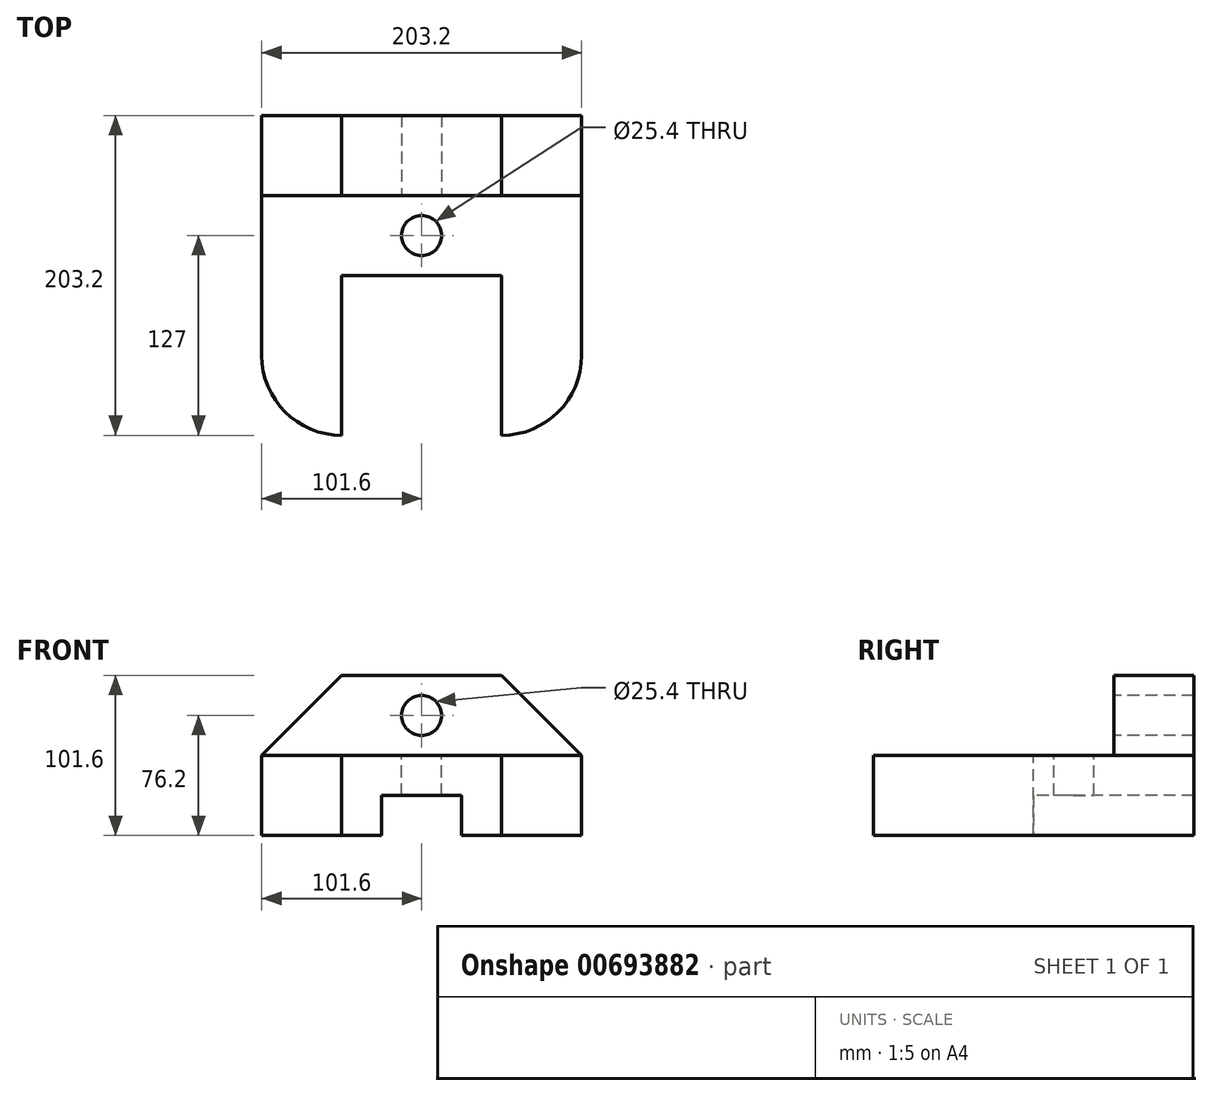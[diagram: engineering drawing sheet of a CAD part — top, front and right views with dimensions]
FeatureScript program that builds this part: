
annotation { "Feature Type Name" : "Feature", "Feature Type Description" : "" }
export const myFeature = defineFeature(function(context is Context, id is Id, definition is map)
    precondition{}
    {
        {
            var Q0;
            Q0=qCreatedBy(makeId("Front.planeOp"),FACE);
            var sketch = newSketch(context, id + "F0", { "sketchPlane" : qUnion([Q0])});
            skLineSegment(sketch, "E0.bottom", {"start": v(-101.6, -50.8) * mm, "end": v(101.6, -50.8) * mm});
            skLineSegment(sketch, "E0.top", {"start": v(-50.8, 50.8) * mm, "end": v(50.8, 50.8) * mm});
            skLineSegment(sketch, "E0.left", {"start": v(-101.6, -50.8) * mm, "end": v(-101.6, 0) * mm});
            skLineSegment(sketch, "E0.right", {"start": v(101.6, -50.8) * mm, "end": v(101.6, 0) * mm});
            skPoint(sketch, "E0.middle", {"position": v(0, 0) * mm});
            skLineSegment(sketch, "E1.0", {"start": v(-101.6, 0) * mm, "end": v(101.6, 0) * mm});
            skCircle(sketch, "E2", {"center": v(0, 25.4) * mm, "radius": 12.7 * mm});
            skLineSegment(sketch, "E3.0", {"start": v(-50.8, -50.8) * mm, "end": v(-50.8, 0) * mm});
            skLineSegment(sketch, "E4.0", {"start": v(50.8, -50.8) * mm, "end": v(50.8, 0) * mm});
            skLineSegment(sketch, "E5.0", {"start": v(25.4, -25.4) * mm, "end": v(25.4, -25.4) * mm});
            skLineSegment(sketch, "E6.0", {"start": v(-25.4, -25.4) * mm, "end": v(25.4, -25.4) * mm});
            skLineSegment(sketch, "E7", {"start": v(-25.4, -25.4) * mm, "end": v(-25.4, -50.8) * mm});
            skLineSegment(sketch, "E8", {"start": v(25.4, -25.4) * mm, "end": v(25.4, -50.8) * mm});
            skLineSegment(sketch, "E9", {"start": v(-101.6, 0) * mm, "end": v(-50.8, 50.8) * mm});
            skLineSegment(sketch, "E10", {"start": v(-50.8, 50.8) * mm, "end": v(-50.8, 0) * mm});
            skLineSegment(sketch, "E11", {"start": v(-50.8, 0) * mm, "end": v(-101.6, 0) * mm});
            skLineSegment(sketch, "E12.MirrorCS", {"start": v(50.8, 50.8) * mm, "end": v(50.8, 0) * mm});
            skLineSegment(sketch, "E13.MirrorCS", {"start": v(101.6, 0) * mm, "end": v(50.8, 50.8) * mm});
            skPoint(sketch, "E14.orphan", {"position": v(-101.6, 50.8) * mm});
            skPoint(sketch, "E15.orphan", {"position": v(101.6, 50.8) * mm});
            skSolve(sketch);
        }
        {
            var Q0;
            Q0=qCreatedBy(makeId("Top.planeOp"),FACE);
            var sketch = newSketch(context, id + "F1", { "sketchPlane" : qUnion([Q0])});
            skLineSegment(sketch, "E16.bottom", {"start": v(-50.8, -101.6) * mm, "end": v(-50.8, -101.6) * mm});
            skLineSegment(sketch, "E16.top", {"start": v(-101.6, 101.6) * mm, "end": v(101.6, 101.6) * mm});
            skLineSegment(sketch, "E16.left", {"start": v(-101.6, -50.8) * mm, "end": v(-101.6, 101.6) * mm});
            skLineSegment(sketch, "E16.right", {"start": v(101.6, -50.8) * mm, "end": v(101.6, 101.6) * mm});
            skPoint(sketch, "E16.middle", {"position": v(0, 0) * mm});
            skLineSegment(sketch, "E17.0", {"start": v(-101.6, 50.8) * mm, "end": v(101.6, 50.8) * mm});
            skLineSegment(sketch, "E18.0", {"start": v(-50.8, 0) * mm, "end": v(50.8, 0) * mm});
            skLineSegment(sketch, "E19.0", {"start": v(-50.8, -101.6) * mm, "end": v(-50.8, 0) * mm});
            skArc(sketch, "E20", {"start": v(-101.6, -50.28) * mm, "mid": v(-86.9, -86.54) * mm, "end": v(-50.8, -101.6) * mm});
            skArc(sketch, "E21.MirrorCS", {"start": v(101.6, -50.28) * mm, "mid": v(86.9, -86.54) * mm, "end": v(50.8, -101.6) * mm});
            skLineSegment(sketch, "E22.trimOffspring", {"start": v(-50.8, 50.8) * mm, "end": v(-50.8, 101.6) * mm});
            skPoint(sketch, "E23.orphan", {"position": v(-101.6, -101.6) * mm});
            skLineSegment(sketch, "E24", {"start": v(50.8, -101.6) * mm, "end": v(50.8, -50.8) * mm});
            skLineSegment(sketch, "E25", {"start": v(50.8, 0) * mm, "end": v(-50.8, 0) * mm});
            skLineSegment(sketch, "E26", {"start": v(50.8, 0) * mm, "end": v(50.8, -50.8) * mm});
            skPoint(sketch, "E27.orphan", {"position": v(101.6, -101.6) * mm});
            skLineSegment(sketch, "E28.trimOffspring", {"start": v(50.8, -101.6) * mm, "end": v(50.8, -101.6) * mm});
            skLineSegment(sketch, "E29.MirrorCS", {"start": v(50.8, 50.8) * mm, "end": v(50.8, 101.6) * mm});
            skCircle(sketch, "E30", {"center": v(0, 25.4) * mm, "radius": 12.7 * mm});
            skSolve(sketch);
        }
        {
            var Q0;
            {var subQ7=sQuery(id+"F1.wireOp",EDGE,"E19.0");Q0=makeQuery(id+"F1.imprint","IMPRINT",FACE,{"disambiguationData":[TD([[makeQuery(id+"F1.imprint","IMPRINT",EDGE,{"derivedFrom":subQ7}),1.0]])]});}
            var Q1;
            {var subQ3=sQuery(id+"F1.wireOp",EDGE,"E22.trimOffspring");Q1=makeQuery(id+"F1.imprint","IMPRINT",FACE,{"disambiguationData":[TD([[makeQuery(id+"F1.imprint","IMPRINT",EDGE,{"derivedFrom":subQ3}),1.0]])]});}
            var Q2;
            {var subQ0=sQuery(id+"F1.wireOp",EDGE,"E22.trimOffspring");Q2=makeQuery(id+"F1.imprint","IMPRINT",FACE,{"disambiguationData":[TD([[makeQuery(id+"F1.imprint","IMPRINT",EDGE,{"derivedFrom":subQ0}),-1.0]])]});}
            var Q3;
            {var subQ3=sQuery(id+"F1.wireOp",EDGE,"E29.MirrorCS");Q3=makeQuery(id+"F1.imprint","IMPRINT",FACE,{"disambiguationData":[TD([[makeQuery(id+"F1.imprint","IMPRINT",EDGE,{"derivedFrom":subQ3}),-1.0]])]});}
            extrude(context, id + "F2", {"entities" : qUnion([Q0, Q1, Q2, Q3]), "oppositeDirection" : true, "depth" : 50.8 * mm, "offsetDistance" : 25.4 * mm});
        }
        {
            var Q0;
            Q0=makeQuery(id+"F0.imprint","IMPRINT",FACE,{"disambiguationData":[TD([[makeQuery(id+"F0.imprint","IMPRINT",EDGE,{"derivedFrom":sQuery(id+"F0.wireOp",EDGE,"E9")}),-1.0]])]});
            var Q1;
            Q1=makeQuery(id+"F0.imprint","IMPRINT",FACE,{"disambiguationData":[TD([[makeQuery(id+"F0.imprint","IMPRINT",EDGE,{"derivedFrom":sQuery(id+"F0.wireOp",EDGE,"E0.top")}),-1.0]])]});
            var Q2;
            {var subQ2=sQuery(id+"F0.wireOp",EDGE,"E12.MirrorCS");Q2=makeQuery(id+"F0.imprint","IMPRINT",FACE,{"disambiguationData":[TD([[makeQuery(id+"F0.imprint","IMPRINT",EDGE,{"derivedFrom":subQ2}),1.0]])]});}
            extrude(context, id + "F3", {"entities" : qUnion([Q0, Q1, Q2]), "operationType" : NewBodyOperationType.ADD, "oppositeDirection" : true, "depth" : 101.6 * mm, "offsetDistance" : 25.4 * mm});
        }
        {
            var Q0;
            Q0=makeQuery(id+"F0.imprint","IMPRINT",FACE,{"disambiguationData":[TD([[makeQuery(id+"F0.imprint","IMPRINT",EDGE,{"derivedFrom":sQuery(id+"F0.wireOp",EDGE,"E0.top")}),-1.0]])]});
            var Q1;
            Q1=makeQuery(id+"F0.imprint","IMPRINT",FACE,{"disambiguationData":[TD([[makeQuery(id+"F0.imprint","IMPRINT",EDGE,{"derivedFrom":sQuery(id+"F0.wireOp",EDGE,"E9")}),-1.0]])]});
            var Q2;
            {var subQ2=sQuery(id+"F0.wireOp",EDGE,"E12.MirrorCS");Q2=makeQuery(id+"F0.imprint","IMPRINT",FACE,{"disambiguationData":[TD([[makeQuery(id+"F0.imprint","IMPRINT",EDGE,{"derivedFrom":subQ2}),1.0]])]});}
            extrude(context, id + "F4", {"entities" : qUnion([Q0, Q1, Q2]), "operationType" : NewBodyOperationType.REMOVE, "oppositeDirection" : true, "depth" : 50.8 * mm, "offsetDistance" : 25.4 * mm});
        }
        {
            var Q0;
            Q0=makeQuery(id+"F0.imprint","IMPRINT",FACE,{"disambiguationData":[TD([[makeQuery(id+"F0.imprint","IMPRINT",EDGE,{"derivedFrom":sQuery(id+"F0.wireOp",EDGE,"E6.0")}),-1.0]])]});
            extrude(context, id + "F5", {"entities" : qUnion([Q0]), "operationType" : NewBodyOperationType.REMOVE, "oppositeDirection" : true, "depth" : 178.82 * mm, "offsetDistance" : 25.4 * mm});
        }
    });
